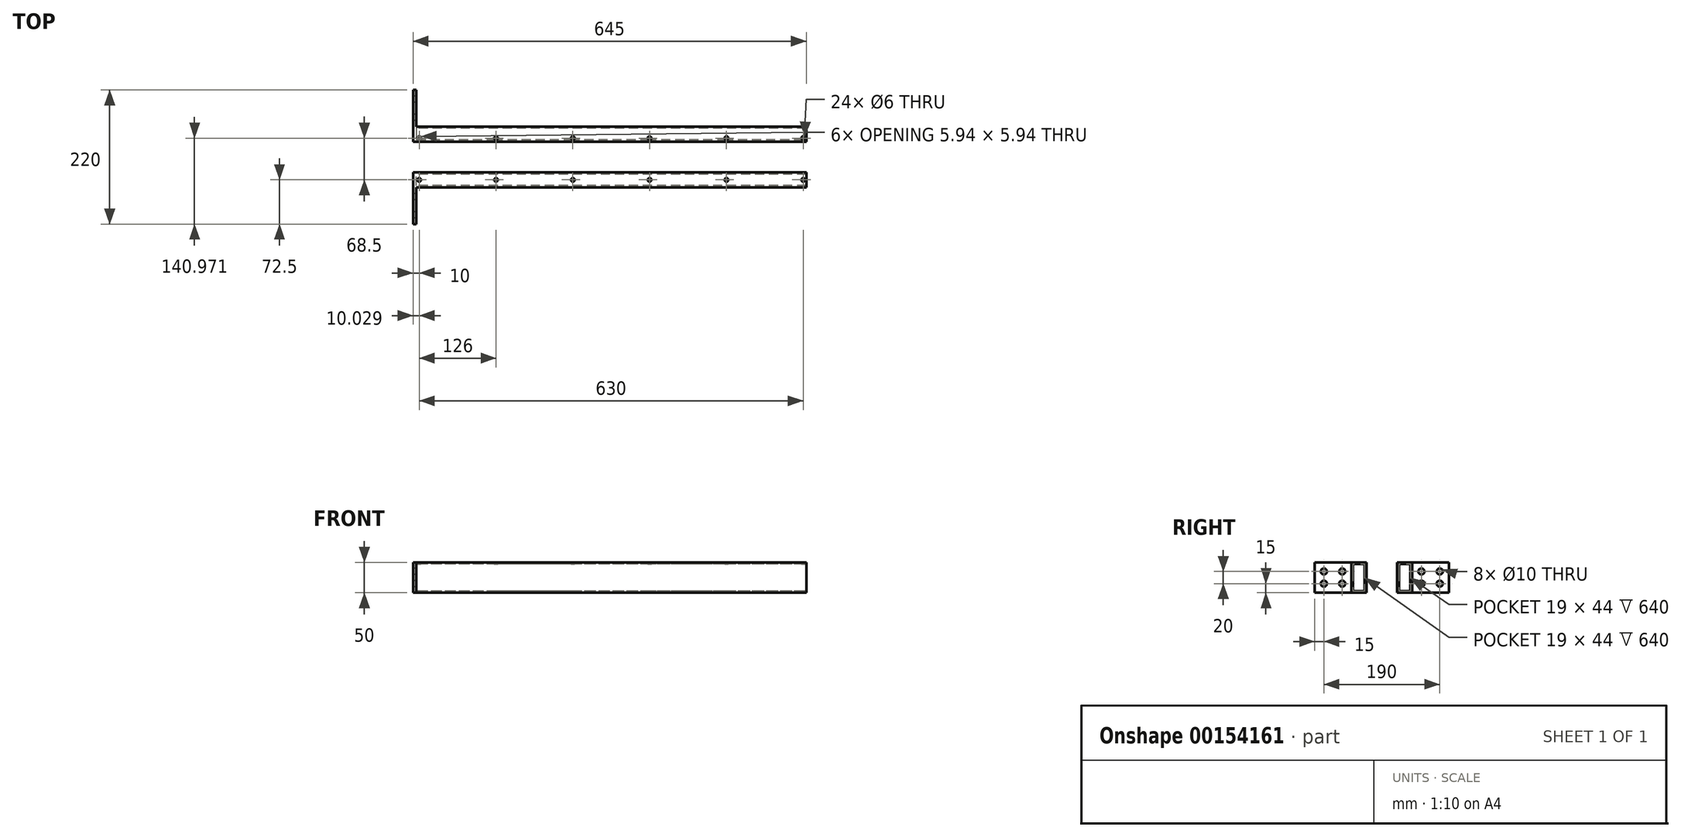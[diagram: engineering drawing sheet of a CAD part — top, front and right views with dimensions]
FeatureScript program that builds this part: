
annotation { "Feature Type Name" : "Feature", "Feature Type Description" : "" }
export const myFeature = defineFeature(function(context is Context, id is Id, definition is map)
    precondition{}
    {
        {
            var Q0;
            Q0=qCreatedBy(makeId("Front.planeOp"),FACE);
            var sketch = newSketch(context, id + "F0", { "sketchPlane" : qUnion([Q0])});
            skLineSegment(sketch, "E0.bottom", {"start": v(320, 25) * mm, "end": v(-320, 25) * mm});
            skLineSegment(sketch, "E0.top", {"start": v(320, -25) * mm, "end": v(-320, -25) * mm});
            skLineSegment(sketch, "E0.left", {"start": v(320, 25) * mm, "end": v(320, -25) * mm});
            skLineSegment(sketch, "E0.right", {"start": v(-320, 25) * mm, "end": v(-320, -25) * mm});
            skPoint(sketch, "E0.middle", {"position": v(0, 0) * mm});
            skSolve(sketch);
        }
        {
            var Q0;
            Q0 = qSketchRegion(id + "F0", true);
            extrude(context, id + "F1", {"entities" : qUnion([Q0]), "depth" : 25 * mm});
        }
        {
            var Q0;
            Q0=makeQuery(id+"F1.opExtrude","SWEPT_FACE",FACE,{"disambiguationData":[OSD([sQuery(id+"F0.wireOp",EDGE,"E0.right")])]});
            var sketch = newSketch(context, id + "F2", { "sketchPlane" : qUnion([Q0])});
            skLineSegment(sketch, "E1.0", {"start": v(22, 22) * mm, "end": v(3, 22) * mm});
            skLineSegment(sketch, "E1.1", {"start": v(22, 22) * mm, "end": v(22, -22) * mm});
            skLineSegment(sketch, "E1.2", {"start": v(22, -22) * mm, "end": v(3, -22) * mm});
            skLineSegment(sketch, "E2.0", {"start": v(3, 22) * mm, "end": v(3, -22) * mm});
            skSolve(sketch);
        }
        {
            var Q0;
            Q0 = qSketchRegion(id + "F2", true);
            extrude(context, id + "F3", {"entities" : qUnion([Q0]), "operationType" : NewBodyOperationType.REMOVE, "oppositeDirection" : true, "depth" : 1130 * mm});
        }
        {
            var Q0;
            Q0=makeQuery(id+"F1.opExtrude","SWEPT_FACE",FACE,{"disambiguationData":[OSD([sQuery(id+"F0.wireOp",EDGE,"E0.right")])]});
            var sketch = newSketch(context, id + "F4", { "sketchPlane" : qUnion([Q0])});
            skPoint(sketch, "E3", {"position": v(0, 25) * mm});
            skLineSegment(sketch, "E4.bottom", {"start": v(0, 25) * mm, "end": v(85, 25) * mm});
            skLineSegment(sketch, "E4.top", {"start": v(0, -25) * mm, "end": v(85, -25) * mm});
            skLineSegment(sketch, "E4.left", {"start": v(0, 25) * mm, "end": v(0, -25) * mm});
            skLineSegment(sketch, "E4.right", {"start": v(85, 25) * mm, "end": v(85, -25) * mm});
            skSolve(sketch);
        }
        {
            var Q0;
            Q0 = qSketchRegion(id + "F4", true);
            extrude(context, id + "F5", {"entities" : qUnion([Q0]), "operationType" : NewBodyOperationType.ADD, "depth" : 5 * mm});
        }
        {
            var Q0;
            Q0=makeQuery(id+"F5.opExtrude","CAP_FACE",FACE,{"disambiguationData":[OSD([sQuery(id+"F4.wireOp",EDGE,"E4.bottom"),sQuery(id+"F4.wireOp",EDGE,"E4.top"),sQuery(id+"F4.wireOp",EDGE,"E4.left"),sQuery(id+"F4.wireOp",EDGE,"E4.right")])],"isStart":false});
            var sketch = newSketch(context, id + "F6", { "sketchPlane" : qUnion([Q0])});
            skLineSegment(sketch, "E5.0", {"start": v(110, 25) * mm, "end": v(25, 25) * mm});
            skLineSegment(sketch, "E6.bottom", {"start": v(25, 25) * mm, "end": v(85, 25) * mm});
            skLineSegment(sketch, "E6.top", {"start": v(25, -25) * mm, "end": v(85, -25) * mm});
            skLineSegment(sketch, "E6.left", {"start": v(25, 25) * mm, "end": v(25, -25) * mm});
            skLineSegment(sketch, "E6.right", {"start": v(85, 25) * mm, "end": v(85, -25) * mm});
            skPoint(sketch, "E7", {"position": v(40, 10) * mm});
            skPoint(sketch, "E8", {"position": v(70, 10) * mm});
            skPoint(sketch, "E9", {"position": v(40, -10) * mm});
            skPoint(sketch, "E10", {"position": v(70, -10) * mm});
            skCircle(sketch, "E11", {"center": v(40, 10) * mm, "radius": 5 * mm});
            skCircle(sketch, "E12", {"center": v(40, -10) * mm, "radius": 5 * mm});
            skCircle(sketch, "E13", {"center": v(70, -10) * mm, "radius": 5 * mm});
            skCircle(sketch, "E14", {"center": v(70, 10) * mm, "radius": 5 * mm});
            skSolve(sketch);
        }
        {
            var Q0;
            Q0=makeQuery(id+"F6.imprint","IMPRINT",FACE,{"disambiguationData":[TD([[makeQuery(id+"F6.imprint","IMPRINT",EDGE,{"derivedFrom":sQuery(id+"F6.wireOp",EDGE,"E12")}),1.0]])]});
            var Q1;
            Q1=makeQuery(id+"F6.imprint","IMPRINT",FACE,{"disambiguationData":[TD([[makeQuery(id+"F6.imprint","IMPRINT",EDGE,{"derivedFrom":sQuery(id+"F6.wireOp",EDGE,"E11")}),1.0]])]});
            var Q2;
            Q2=makeQuery(id+"F6.imprint","IMPRINT",FACE,{"disambiguationData":[TD([[makeQuery(id+"F6.imprint","IMPRINT",EDGE,{"derivedFrom":sQuery(id+"F6.wireOp",EDGE,"E14")}),1.0]])]});
            var Q3;
            Q3=makeQuery(id+"F6.imprint","IMPRINT",FACE,{"disambiguationData":[TD([[makeQuery(id+"F6.imprint","IMPRINT",EDGE,{"derivedFrom":sQuery(id+"F6.wireOp",EDGE,"E13")}),1.0]])]});
            extrude(context, id + "F7", {"entities" : qUnion([Q0, Q1, Q2, Q3]), "operationType" : NewBodyOperationType.REMOVE, "oppositeDirection" : true, "depth" : 5 * mm});
        }
        {
            var Q0;
            Q0=qCreatedBy(makeId("Front.planeOp"),FACE);
            cPlane(context, id + "F8", {"entities" : qUnion([Q0]), "cplaneType" : CPlaneType.OFFSET, "offset" : 25 * mm, "oppositeDirection" : true, "width" : 150 * mm, "height" : 150 * mm});
        }
        {
            var Q0;
            Q0=makeQuery(id+"F1.opExtrude","SWEPT_BODY",BODY,{"disambiguationData":[OSD([sQuery(id+"F0.wireOp",EDGE,"E0.bottom"),sQuery(id+"F0.wireOp",EDGE,"E0.top"),sQuery(id+"F0.wireOp",EDGE,"E0.left"),sQuery(id+"F0.wireOp",EDGE,"E0.right")])]});
            var Q1;
            Q1=qCreatedBy(id+"F8.planeOp",FACE);
            mirror(context, id + "F9", {"entities" : qUnion([Q0]), "mirrorPlane" : qUnion([Q1])});
        }
        {
            var Q0;
            {var subQ0=sQuery(id+"F4.wireOp",EDGE,"E4.bottom");Q0=makeQuery(id+"F4GclaWFLD7ojnU_1.1.F5.boolean.opBoolean","MERGE",FACE,{"derivedFrom":[makeQuery(id+"F5.boolean.opBoolean","MERGE",FACE,{"derivedFrom":[makeQuery(id+"F1.opExtrude","SWEPT_FACE",FACE,{"disambiguationData":[OSD([sQuery(id+"F0.wireOp",EDGE,"E0.bottom")])]}),makeQuery(id+"F5.opExtrude","SWEPT_FACE",FACE,{"disambiguationData":[OSD([subQ0])]})]}),makeQuery(id+"F4GclaWFLD7ojnU_1.1.F5.opExtrude","SWEPT_FACE",FACE,{"disambiguationData":[OSD([subQ0])]})]});}
            var sketch = newSketch(context, id + "F10", { "sketchPlane" : qUnion([Q0])});
            skPoint(sketch, "E15", {"position": v(325, -12.5) * mm});
            skPoint(sketch, "E16", {"position": v(315, -12.5) * mm});
            skPoint(sketch, "E17", {"position": v(189, -12.5) * mm});
            skPoint(sketch, "E18", {"position": v(63, -12.5) * mm});
            skPoint(sketch, "E19", {"position": v(-63, -12.5) * mm});
            skPoint(sketch, "E20", {"position": v(-189, -12.5) * mm});
            skPoint(sketch, "E21", {"position": v(-315, -12.5) * mm});
            skCircle(sketch, "E22", {"center": v(-315, -12.5) * mm, "radius": 3 * mm});
            skCircle(sketch, "E23", {"center": v(-189, -12.5) * mm, "radius": 3 * mm});
            skCircle(sketch, "E24", {"center": v(-63, -12.5) * mm, "radius": 3 * mm});
            skCircle(sketch, "E25", {"center": v(63, -12.5) * mm, "radius": 3 * mm});
            skCircle(sketch, "E26", {"center": v(189, -12.5) * mm, "radius": 3 * mm});
            skCircle(sketch, "E27", {"center": v(315, -12.5) * mm, "radius": 3 * mm});
            skSolve(sketch);
        }
        {
            var Q0;
            Q0 = qSketchRegion(id + "F10", true);
            extrude(context, id + "F11", {"entities" : qUnion([Q0]), "operationType" : NewBodyOperationType.REMOVE, "oppositeDirection" : true, "depth" : 50 * mm});
        }
        {
            var Q0;
            {var subQ0=sQuery(id+"F4.wireOp",EDGE,"E4.bottom");Q0=makeQuery(id+"F9.opPattern","COPY",FACE,{"derivedFrom":makeQuery(id+"F4GclaWFLD7ojnU_1.1.F5.boolean.opBoolean","MERGE",FACE,{"derivedFrom":[makeQuery(id+"F5.boolean.opBoolean","MERGE",FACE,{"derivedFrom":[makeQuery(id+"F1.opExtrude","SWEPT_FACE",FACE,{"disambiguationData":[OSD([sQuery(id+"F0.wireOp",EDGE,"E0.bottom")])]}),makeQuery(id+"F5.opExtrude","SWEPT_FACE",FACE,{"disambiguationData":[OSD([subQ0])]})]}),makeQuery(id+"F4GclaWFLD7ojnU_1.1.F5.opExtrude","SWEPT_FACE",FACE,{"disambiguationData":[OSD([subQ0])]})]}),"instanceName":"1"});}
            var sketch = newSketch(context, id + "F12", { "sketchPlane" : qUnion([Q0])});
            skPoint(sketch, "E28", {"position": v(325, 56) * mm});
            skPoint(sketch, "E29", {"position": v(315, 56) * mm});
            skPoint(sketch, "E30", {"position": v(189, 56) * mm});
            skPoint(sketch, "E31", {"position": v(63, 56) * mm});
            skPoint(sketch, "E32", {"position": v(-63, 56) * mm});
            skPoint(sketch, "E33", {"position": v(-189, 56) * mm});
            skPoint(sketch, "E34", {"position": v(-315, 56) * mm});
            skCircle(sketch, "E35", {"center": v(-315, 56) * mm, "radius": 3 * mm});
            skCircle(sketch, "E36", {"center": v(-189, 56) * mm, "radius": 3 * mm});
            skCircle(sketch, "E37", {"center": v(-63, 56) * mm, "radius": 3 * mm});
            skCircle(sketch, "E38", {"center": v(63, 56) * mm, "radius": 3 * mm});
            skCircle(sketch, "E39", {"center": v(189, 56) * mm, "radius": 3 * mm});
            skCircle(sketch, "E40", {"center": v(315, 56) * mm, "radius": 3 * mm});
            skSolve(sketch);
        }
        {
            var Q0;
            Q0 = qSketchRegion(id + "F12", true);
            extrude(context, id + "F13", {"entities" : qUnion([Q0]), "operationType" : NewBodyOperationType.REMOVE, "oppositeDirection" : true, "depth" : 50 * mm});
        }
    });
